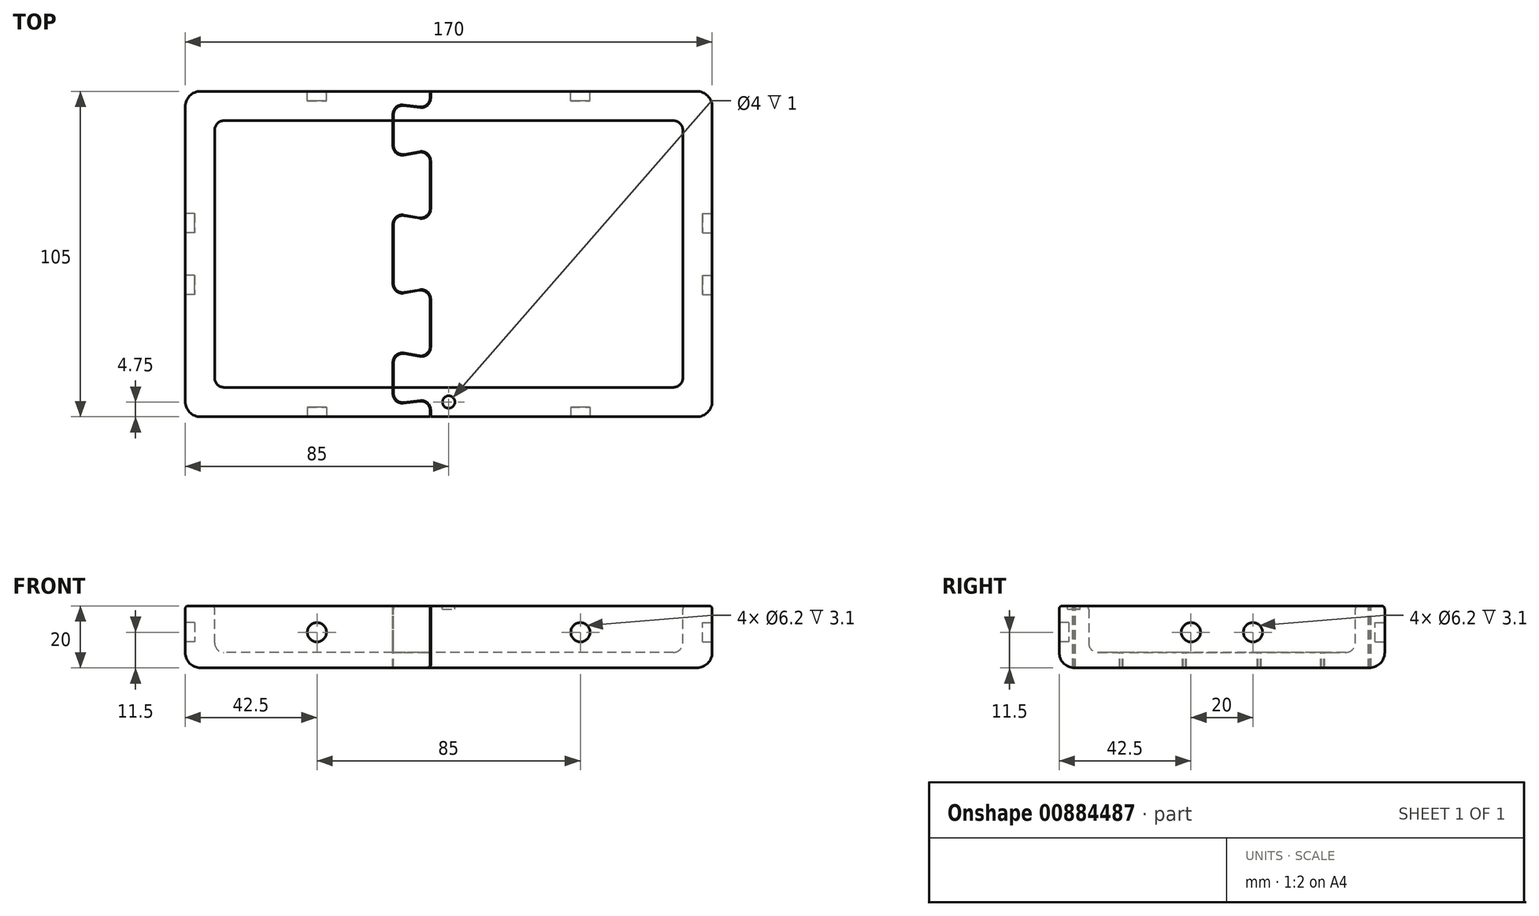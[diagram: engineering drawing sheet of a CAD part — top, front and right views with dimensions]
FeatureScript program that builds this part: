
annotation { "Feature Type Name" : "Feature", "Feature Type Description" : "" }
export const myFeature = defineFeature(function(context is Context, id is Id, definition is map)
    precondition{}
    {
        {
            var Q0;
            Q0=qCreatedBy(makeId("Top.planeOp"),FACE);
            var sketch = newSketch(context, id + "F0", { "sketchPlane" : qUnion([Q0])});
            skLineSegment(sketch, "E0.bottom", {"start": v(-85, 52.5) * mm, "end": v(85, 52.5) * mm});
            skLineSegment(sketch, "E0.top", {"start": v(-85, -52.5) * mm, "end": v(85, -52.5) * mm});
            skLineSegment(sketch, "E0.left", {"start": v(-85, 52.5) * mm, "end": v(-85, -52.5) * mm});
            skLineSegment(sketch, "E0.right", {"start": v(85, 52.5) * mm, "end": v(85, -52.5) * mm});
            skLineSegment(sketch, "E1.bottom", {"start": v(-72.5, 43) * mm, "end": v(72.5, 43) * mm});
            skLineSegment(sketch, "E1.top", {"start": v(-72.5, -43) * mm, "end": v(72.5, -43) * mm});
            skLineSegment(sketch, "E1.left", {"start": v(-75.5, 40) * mm, "end": v(-75.5, -40) * mm});
            skLineSegment(sketch, "E1.right", {"start": v(75.5, 40) * mm, "end": v(75.5, -40) * mm});
            skLineSegment(sketch, "E2.direction1", {"start": v(-75.5, -43) * mm, "end": v(15.26, -43) * mm, "construction": true});
            skPoint(sketch, "E3.visualSharp", {"position": v(-75.5, 43) * mm});
            skArc(sketch, "E3.filletArc", {"start": v(-72.5, 43) * mm, "mid": v(-74.62, 42.12) * mm, "end": v(-75.5, 40) * mm});
            skPoint(sketch, "E4.visualSharp", {"position": v(75.5, 43) * mm});
            skArc(sketch, "E4.filletArc", {"start": v(75.5, 40) * mm, "mid": v(74.62, 42.12) * mm, "end": v(72.5, 43) * mm});
            skPoint(sketch, "E5.visualSharp", {"position": v(75.5, -43) * mm});
            skArc(sketch, "E5.filletArc", {"start": v(72.5, -43) * mm, "mid": v(74.62, -42.12) * mm, "end": v(75.5, -40) * mm});
            skPoint(sketch, "E6.visualSharp", {"position": v(-75.5, -43) * mm});
            skArc(sketch, "E6.filletArc", {"start": v(-75.5, -40) * mm, "mid": v(-74.62, -42.12) * mm, "end": v(-72.5, -43) * mm});
            skLineSegment(sketch, "E7.direction1", {"start": v(-75.5, -43) * mm, "end": v(17, -43) * mm, "construction": true});
            skLineSegment(sketch, "E8", {"start": v(-85, 0) * mm, "end": v(85, 0) * mm, "construction": true});
            skLineSegment(sketch, "E9", {"start": v(0, -52.5) * mm, "end": v(0, 52.5) * mm, "construction": true});
            skCircle(sketch, "E10", {"center": v(0, -47.75) * mm, "radius": 2 * mm});
            skSolve(sketch);
        }
        {
            assignVariable(context, id + "F1", {"name" : "h", "anyValue" : 20});
        }
        {
            assignVariable(context, id + "F2", {"name" : "d", "anyValue" : 15});
        }
        {
            var Q0;
            Q0=makeQuery(id+"F0.imprint","IMPRINT",FACE,{"disambiguationData":[TD([[makeQuery(id+"F0.imprint","IMPRINT",EDGE,{"derivedFrom":sQuery(id+"F0.wireOp",EDGE,"E1.bottom")}),-1.0]])]});
            var Q1;
            Q1=makeQuery(id+"F0.imprint","IMPRINT",FACE,{"disambiguationData":[TD([[makeQuery(id+"F0.imprint","IMPRINT",EDGE,{"derivedFrom":sQuery(id+"F0.wireOp",EDGE,"E0.bottom")}),-1.0]])]});
            var Q2;
            Q2=makeQuery(id+"F0.imprint","IMPRINT",FACE,{"disambiguationData":[TD([[makeQuery(id+"F0.imprint","IMPRINT",EDGE,{"derivedFrom":sQuery(id+"F0.wireOp",EDGE,"E2.0.2.0")}),1.0]])]});
            var Q3;
            Q3=makeQuery(id+"F0.imprint","IMPRINT",FACE,{"disambiguationData":[TD([[makeQuery(id+"F0.imprint","IMPRINT",EDGE,{"derivedFrom":sQuery(id+"F0.wireOp",EDGE,"E2.0.3.0")}),1.0]])]});
            var Q4;
            Q4=makeQuery(id+"F0.imprint","IMPRINT",FACE,{"disambiguationData":[TD([[makeQuery(id+"F0.imprint","IMPRINT",EDGE,{"derivedFrom":sQuery(id+"F0.wireOp",EDGE,"E2.0.1.0")}),1.0]])]});
            var Q5;
            Q5=makeQuery(id+"F0.imprint","IMPRINT",FACE,{"disambiguationData":[TD([[makeQuery(id+"F0.imprint","IMPRINT",EDGE,{"derivedFrom":sQuery(id+"F0.wireOp",EDGE,"E7.0.1.2")}),1.0]])]});
            var Q6;
            Q6=makeQuery(id+"F0.imprint","IMPRINT",FACE,{"disambiguationData":[TD([[makeQuery(id+"F0.imprint","IMPRINT",EDGE,{"derivedFrom":sQuery(id+"F0.wireOp",EDGE,"E7.0.2.2")}),1.0]])]});
            var Q7;
            Q7=makeQuery(id+"F0.imprint","IMPRINT",FACE,{"disambiguationData":[TD([[makeQuery(id+"F0.imprint","IMPRINT",EDGE,{"derivedFrom":sQuery(id+"F0.wireOp",EDGE,"E7.0.3.2")}),1.0]])]});
            var Q8;
            Q8=makeQuery(id+"F0.imprint","IMPRINT",FACE,{"disambiguationData":[TD([[makeQuery(id+"F0.imprint","IMPRINT",EDGE,{"derivedFrom":sQuery(id+"F0.wireOp",EDGE,"E10")}),1.0]])]});
            extrude(context, id + "F3", {"entities" : qUnion([Q0, Q1, Q2, Q3, Q4, Q5, Q6, Q7, Q8]), "depth" : (getVariable(context, 'h')) * mm, "offsetDistance" : 25 * mm});
        }
        {
            var Q0;
            Q0=makeQuery(id+"F0.imprint","IMPRINT",FACE,{"disambiguationData":[TD([[makeQuery(id+"F0.imprint","IMPRINT",EDGE,{"derivedFrom":sQuery(id+"F0.wireOp",EDGE,"E1.bottom")}),-1.0]])]});
            var Q1;
            Q1=makeQuery(id+"F0.imprint","IMPRINT",FACE,{"disambiguationData":[TD([[makeQuery(id+"F0.imprint","IMPRINT",EDGE,{"derivedFrom":sQuery(id+"F0.wireOp",EDGE,"E2.0.1.0")}),1.0]])]});
            var Q2;
            Q2=makeQuery(id+"F0.imprint","IMPRINT",FACE,{"disambiguationData":[TD([[makeQuery(id+"F0.imprint","IMPRINT",EDGE,{"derivedFrom":sQuery(id+"F0.wireOp",EDGE,"E2.0.2.0")}),1.0]])]});
            var Q3;
            Q3=makeQuery(id+"F0.imprint","IMPRINT",FACE,{"disambiguationData":[TD([[makeQuery(id+"F0.imprint","IMPRINT",EDGE,{"derivedFrom":sQuery(id+"F0.wireOp",EDGE,"E2.0.3.0")}),1.0]])]});
            var Q4;
            Q4=makeQuery(id+"F0.imprint","IMPRINT",FACE,{"disambiguationData":[TD([[makeQuery(id+"F0.imprint","IMPRINT",EDGE,{"derivedFrom":sQuery(id+"F0.wireOp",EDGE,"E7.0.1.2")}),1.0]])]});
            var Q5;
            Q5=makeQuery(id+"F0.imprint","IMPRINT",FACE,{"disambiguationData":[TD([[makeQuery(id+"F0.imprint","IMPRINT",EDGE,{"derivedFrom":sQuery(id+"F0.wireOp",EDGE,"E7.0.2.2")}),1.0]])]});
            var Q6;
            Q6=makeQuery(id+"F0.imprint","IMPRINT",FACE,{"disambiguationData":[TD([[makeQuery(id+"F0.imprint","IMPRINT",EDGE,{"derivedFrom":sQuery(id+"F0.wireOp",EDGE,"E7.0.3.2")}),1.0]])]});
            extrude(context, id + "F4", {"entities" : qUnion([Q0, Q1, Q2, Q3, Q4, Q5, Q6]), "operationType" : NewBodyOperationType.REMOVE, "depth" : (getVariable(context, 'd')) * mm, "offsetDistance" : 25 * mm});
        }
        {
            var Q0;
            Q0=makeQuery(id+"F3.opExtrude","CAP_FACE",FACE,{"disambiguationData":[OSD([sQuery(id+"F0.wireOp",EDGE,"E0.bottom"),sQuery(id+"F0.wireOp",EDGE,"E0.top"),sQuery(id+"F0.wireOp",EDGE,"E0.left"),sQuery(id+"F0.wireOp",EDGE,"E0.right")])],"isStart":false});
            var Q1;
            Q1=makeQuery(id+"F3.opExtrude","SWEPT_EDGE",EDGE,{"disambiguationData":[OSD([sQuery(id+"F0.wireOp",EDGE,"E0.bottom"),sQuery(id+"F0.wireOp",EDGE,"E0.right")])]});
            var Q2;
            Q2=makeQuery(id+"F3.opExtrude","SWEPT_EDGE",EDGE,{"disambiguationData":[OSD([sQuery(id+"F0.wireOp",EDGE,"E0.bottom"),sQuery(id+"F0.wireOp",EDGE,"E0.left")])]});
            var Q3;
            Q3=makeQuery(id+"F3.opExtrude","SWEPT_EDGE",EDGE,{"disambiguationData":[OSD([sQuery(id+"F0.wireOp",EDGE,"E0.top"),sQuery(id+"F0.wireOp",EDGE,"E0.left")])]});
            var Q4;
            Q4=makeQuery(id+"F3.opExtrude","SWEPT_EDGE",EDGE,{"disambiguationData":[OSD([sQuery(id+"F0.wireOp",EDGE,"E0.top"),sQuery(id+"F0.wireOp",EDGE,"E0.right")])]});
            fillet(context, id + "F5", {"entities" : qUnion([Q0, Q1, Q2, Q3, Q4]), "radius" : 5 * mm, "tangentPropagation" : true, "allowEdgeOverflow" : false});
        }
        {
            var Q0;
            Q0=makeQuery(id+"F4.boolean.opBoolean","COPY",FACE,{"derivedFrom":makeQuery(id+"F4.opExtrude","CAP_FACE",FACE,{"disambiguationData":[OSD([sQuery(id+"F0.wireOp",EDGE,"E1.bottom"),sQuery(id+"F0.wireOp",EDGE,"E1.top"),sQuery(id+"F0.wireOp",EDGE,"E1.left"),sQuery(id+"F0.wireOp",EDGE,"E1.right"),sQuery(id+"F0.wireOp",EDGE,"E3.filletArc"),sQuery(id+"F0.wireOp",EDGE,"E4.filletArc"),sQuery(id+"F0.wireOp",EDGE,"E5.filletArc"),sQuery(id+"F0.wireOp",EDGE,"E6.filletArc")])],"isStart":false})});
            var Q1;
            Q1=makeQuery(id+"F4.boolean.opBoolean","COPY",FACE,{"derivedFrom":makeQuery(id+"F4.opExtrude","CAP_FACE",FACE,{"disambiguationData":[OSD([sQuery(id+"F0.wireOp",EDGE,"E7.0.1.2"),sQuery(id+"F0.wireOp",EDGE,"E7.0.1.4"),sQuery(id+"F0.wireOp",EDGE,"E7.0.1.5"),sQuery(id+"F0.wireOp",EDGE,"E7.0.1.6"),sQuery(id+"F0.wireOp",EDGE,"E7.0.1.7"),sQuery(id+"F0.wireOp",EDGE,"E7.0.1.9"),sQuery(id+"F0.wireOp",EDGE,"E7.0.1.11"),sQuery(id+"F0.wireOp",EDGE,"E7.0.1.12")])],"isStart":false})});
            var Q2;
            Q2=makeQuery(id+"F4.boolean.opBoolean","COPY",FACE,{"derivedFrom":makeQuery(id+"F4.opExtrude","CAP_FACE",FACE,{"disambiguationData":[OSD([sQuery(id+"F0.wireOp",EDGE,"E7.0.2.2"),sQuery(id+"F0.wireOp",EDGE,"E7.0.2.4"),sQuery(id+"F0.wireOp",EDGE,"E7.0.2.5"),sQuery(id+"F0.wireOp",EDGE,"E7.0.2.6"),sQuery(id+"F0.wireOp",EDGE,"E7.0.2.7"),sQuery(id+"F0.wireOp",EDGE,"E7.0.2.9"),sQuery(id+"F0.wireOp",EDGE,"E7.0.2.11"),sQuery(id+"F0.wireOp",EDGE,"E7.0.2.12")])],"isStart":false})});
            var Q3;
            Q3=makeQuery(id+"F4.boolean.opBoolean","COPY",FACE,{"derivedFrom":makeQuery(id+"F4.opExtrude","CAP_FACE",FACE,{"disambiguationData":[OSD([sQuery(id+"F0.wireOp",EDGE,"E7.0.3.2"),sQuery(id+"F0.wireOp",EDGE,"E7.0.3.4"),sQuery(id+"F0.wireOp",EDGE,"E7.0.3.5"),sQuery(id+"F0.wireOp",EDGE,"E7.0.3.6"),sQuery(id+"F0.wireOp",EDGE,"E7.0.3.7"),sQuery(id+"F0.wireOp",EDGE,"E7.0.3.9"),sQuery(id+"F0.wireOp",EDGE,"E7.0.3.11"),sQuery(id+"F0.wireOp",EDGE,"E7.0.3.12")])],"isStart":false})});
            fillet(context, id + "F6", {"entities" : qUnion([Q0, Q1, Q2, Q3]), "radius" : 3 * mm, "tangentPropagation" : true, "allowEdgeOverflow" : false});
        }
        {
            var Q0;
            Q0=makeQuery(id+"F3.opExtrude","CAP_FACE",FACE,{"disambiguationData":[OSD([sQuery(id+"F0.wireOp",EDGE,"E0.bottom"),sQuery(id+"F0.wireOp",EDGE,"E0.top"),sQuery(id+"F0.wireOp",EDGE,"E0.left"),sQuery(id+"F0.wireOp",EDGE,"E0.right")])],"isStart":true});
            fillet(context, id + "F7", {"entities" : qUnion([Q0]), "radius" : 1 * mm, "tangentPropagation" : true, "allowEdgeOverflow" : false});
        }
        {
            var Q0;
            Q0=makeQuery(id+"F3.opExtrude","SWEPT_FACE",FACE,{"disambiguationData":[OSD([sQuery(id+"F0.wireOp",EDGE,"E0.top")])]});
            var sketch = newSketch(context, id + "F8", { "sketchPlane" : qUnion([Q0])});
            skCircle(sketch, "E11", {"center": v(42.5, 8.5) * mm, "radius": 3.1 * mm});
            skCircle(sketch, "E12", {"center": v(-42.5, 8.5) * mm, "radius": 3.1 * mm});
            skLineSegment(sketch, "E13", {"start": v(-42.5, 8.5) * mm, "end": v(42.5, 8.5) * mm, "construction": true});
            skSolve(sketch);
        }
        {
            var Q0;
            Q0=makeQuery(id+"F8.imprint","IMPRINT",FACE,{"disambiguationData":[TD([[makeQuery(id+"F8.imprint","IMPRINT",EDGE,{"derivedFrom":sQuery(id+"F8.wireOp",EDGE,"E11")}),1.0]])]});
            var Q1;
            Q1=makeQuery(id+"F8.imprint","IMPRINT",FACE,{"disambiguationData":[TD([[makeQuery(id+"F8.imprint","IMPRINT",EDGE,{"derivedFrom":sQuery(id+"F8.wireOp",EDGE,"E12")}),1.0]])]});
            extrude(context, id + "F9", {"entities" : qUnion([Q0, Q1]), "operationType" : NewBodyOperationType.REMOVE, "oppositeDirection" : true, "depth" : 3.1 * mm, "offsetDistance" : 25 * mm});
        }
        {
            var Q0;
            Q0=makeQuery(id+"F3.opExtrude","SWEPT_FACE",FACE,{"disambiguationData":[OSD([sQuery(id+"F0.wireOp",EDGE,"E0.bottom")])]});
            var sketch = newSketch(context, id + "F10", { "sketchPlane" : qUnion([Q0])});
            skCircle(sketch, "E14", {"center": v(42.5, 8.5) * mm, "radius": 3.1 * mm});
            skCircle(sketch, "E15", {"center": v(-42.5, 8.5) * mm, "radius": 3.1 * mm});
            skLineSegment(sketch, "E16", {"start": v(42.5, 8.5) * mm, "end": v(-42.5, 8.5) * mm, "construction": true});
            skSolve(sketch);
        }
        {
            var Q0;
            Q0=makeQuery(id+"F10.imprint","IMPRINT",FACE,{"disambiguationData":[TD([[makeQuery(id+"F10.imprint","IMPRINT",EDGE,{"derivedFrom":sQuery(id+"F10.wireOp",EDGE,"E14")}),1.0]])]});
            var Q1;
            Q1=makeQuery(id+"F10.imprint","IMPRINT",FACE,{"disambiguationData":[TD([[makeQuery(id+"F10.imprint","IMPRINT",EDGE,{"derivedFrom":sQuery(id+"F10.wireOp",EDGE,"E15")}),1.0]])]});
            extrude(context, id + "F11", {"entities" : qUnion([Q0, Q1]), "operationType" : NewBodyOperationType.REMOVE, "oppositeDirection" : true, "depth" : 3.1 * mm, "offsetDistance" : 25 * mm});
        }
        {
            var Q0;
            Q0=makeQuery(id+"F3.opExtrude","SWEPT_FACE",FACE,{"disambiguationData":[OSD([sQuery(id+"F0.wireOp",EDGE,"E0.left")])]});
            var sketch = newSketch(context, id + "F12", { "sketchPlane" : qUnion([Q0])});
            skCircle(sketch, "E17", {"center": v(10, 8.5) * mm, "radius": 3.1 * mm});
            skCircle(sketch, "E18", {"center": v(-10, 8.5) * mm, "radius": 3.1 * mm});
            skLineSegment(sketch, "E19", {"start": v(-10, 8.5) * mm, "end": v(10, 8.5) * mm, "construction": true});
            skSolve(sketch);
        }
        {
            var Q0;
            Q0=makeQuery(id+"F12.imprint","IMPRINT",FACE,{"disambiguationData":[TD([[makeQuery(id+"F12.imprint","IMPRINT",EDGE,{"derivedFrom":sQuery(id+"F12.wireOp",EDGE,"E17")}),1.0]])]});
            var Q1;
            Q1=makeQuery(id+"F12.imprint","IMPRINT",FACE,{"disambiguationData":[TD([[makeQuery(id+"F12.imprint","IMPRINT",EDGE,{"derivedFrom":sQuery(id+"F12.wireOp",EDGE,"E18")}),1.0]])]});
            extrude(context, id + "F13", {"entities" : qUnion([Q0, Q1]), "operationType" : NewBodyOperationType.REMOVE, "oppositeDirection" : true, "depth" : 3.1 * mm, "offsetDistance" : 25 * mm});
        }
        {
            var Q0;
            Q0=makeQuery(id+"F3.opExtrude","SWEPT_FACE",FACE,{"disambiguationData":[OSD([sQuery(id+"F0.wireOp",EDGE,"E0.right")])]});
            var sketch = newSketch(context, id + "F14", { "sketchPlane" : qUnion([Q0])});
            skCircle(sketch, "E20", {"center": v(10, 8.5) * mm, "radius": 3.1 * mm});
            skCircle(sketch, "E21", {"center": v(-10, 8.5) * mm, "radius": 3.1 * mm});
            skLineSegment(sketch, "E22", {"start": v(10, 8.5) * mm, "end": v(-10, 8.5) * mm, "construction": true});
            skSolve(sketch);
        }
        {
            var Q0;
            Q0=makeQuery(id+"F14.imprint","IMPRINT",FACE,{"disambiguationData":[TD([[makeQuery(id+"F14.imprint","IMPRINT",EDGE,{"derivedFrom":sQuery(id+"F14.wireOp",EDGE,"E20")}),1.0]])]});
            var Q1;
            Q1=makeQuery(id+"F14.imprint","IMPRINT",FACE,{"disambiguationData":[TD([[makeQuery(id+"F14.imprint","IMPRINT",EDGE,{"derivedFrom":sQuery(id+"F14.wireOp",EDGE,"E21")}),1.0]])]});
            extrude(context, id + "F15", {"entities" : qUnion([Q0, Q1]), "operationType" : NewBodyOperationType.REMOVE, "oppositeDirection" : true, "depth" : 3.1 * mm, "offsetDistance" : 25 * mm});
        }
        {
            var Q0;
            Q0=makeQuery(id+"F0.imprint","IMPRINT",FACE,{"disambiguationData":[TD([[makeQuery(id+"F0.imprint","IMPRINT",EDGE,{"derivedFrom":sQuery(id+"F0.wireOp",EDGE,"E10")}),1.0]])]});
            var Q1;
            Q1=sQuery(id+"F0.wireOp",EDGE,"E10");
            extrude(context, id + "F16", {"entities" : qUnion([Q0]), "operationType" : NewBodyOperationType.REMOVE, "surfaceEntities" : qUnion([Q1]), "depth" : 1 * mm, "offsetDistance" : 25 * mm});
        }
        {
            var Q0;
            Q0=makeQuery(id+"F3.opExtrude","SWEPT_BODY",BODY,{"disambiguationData":[OSD([sQuery(id+"F0.wireOp",EDGE,"E0.bottom"),sQuery(id+"F0.wireOp",EDGE,"E0.top"),sQuery(id+"F0.wireOp",EDGE,"E0.left"),sQuery(id+"F0.wireOp",EDGE,"E0.right")])]});
            var Q1;
            Q1=sQuery(id+"F0.wireOp",EDGE,"E9");
            transform(context, id + "F17", {"entities" : qUnion([Q0]), "transformType" : TransformType.ROTATION, "transformAxis" : qUnion([Q1]), "angle" : 180 * degree, "makeCopy" : false});
        }
        {
            var Q0;
            Q0=qCreatedBy(makeId("Top.planeOp"),FACE);
            var sketch = newSketch(context, id + "F18", { "sketchPlane" : qUnion([Q0])});
            skLineSegment(sketch, "E23", {"start": v(-18, 0) * mm, "end": v(-18, 9.66) * mm});
            skLineSegment(sketch, "E24", {"start": v(-14.48, 12.62) * mm, "end": v(-9.52, 11.74) * mm});
            skLineSegment(sketch, "E25", {"start": v(-6, 14.7) * mm, "end": v(-6, 29.85) * mm});
            skLineSegment(sketch, "E26", {"start": v(-9.52, 32.8) * mm, "end": v(-14.48, 31.93) * mm});
            skLineSegment(sketch, "E27", {"start": v(-18, 34.89) * mm, "end": v(-18, 45.12) * mm});
            skLineSegment(sketch, "E28", {"start": v(-14.65, 48.1) * mm, "end": v(-9.35, 47.48) * mm});
            skLineSegment(sketch, "E29", {"start": v(-6, 50.46) * mm, "end": v(-6, 69.12) * mm});
            skLineSegment(sketch, "E30", {"start": v(-6, 69.12) * mm, "end": v(-107.24, 69.12) * mm});
            skLineSegment(sketch, "E31", {"start": v(-107.24, 69.12) * mm, "end": v(-107.24, 0) * mm});
            skLineSegment(sketch, "E32.MirrorCS", {"start": v(-6, -69.12) * mm, "end": v(-107.24, -69.12) * mm});
            skLineSegment(sketch, "E33.MirrorCS", {"start": v(-107.24, -69.12) * mm, "end": v(-107.24, 0) * mm});
            skLineSegment(sketch, "E34", {"start": v(-5.8, 69.12) * mm, "end": v(108.1, 69.12) * mm});
            skLineSegment(sketch, "E35", {"start": v(108.1, 69.12) * mm, "end": v(108.1, -69.12) * mm});
            skLineSegment(sketch, "E36", {"start": v(108.1, -69.12) * mm, "end": v(-5.8, -69.12) * mm});
            skLineSegment(sketch, "E37.0", {"start": v(-5.8, 50.23) * mm, "end": v(-5.8, 69.12) * mm});
            skLineSegment(sketch, "E37.1", {"start": v(-14.45, 47.88) * mm, "end": v(-9.15, 47.25) * mm});
            skLineSegment(sketch, "E37.2", {"start": v(-17.8, 35.13) * mm, "end": v(-17.8, 44.9) * mm});
            skLineSegment(sketch, "E37.3", {"start": v(-17.8, 0) * mm, "end": v(-17.8, 9.42) * mm});
            skLineSegment(sketch, "E37.4", {"start": v(-14.28, 12.38) * mm, "end": v(-9.32, 11.5) * mm});
            skLineSegment(sketch, "E37.5", {"start": v(-5.8, 14.46) * mm, "end": v(-5.8, 30.1) * mm});
            skLineSegment(sketch, "E37.6", {"start": v(-9.32, 33.05) * mm, "end": v(-14.28, 32.17) * mm});
            skPoint(sketch, "E38.visualSharp", {"position": v(-6, 47.08) * mm});
            skArc(sketch, "E38.filletArc", {"start": v(-9.35, 47.48) * mm, "mid": v(-7, 48.21) * mm, "end": v(-6, 50.46) * mm});
            skPoint(sketch, "E39.visualSharp", {"position": v(-5.8, 46.85) * mm});
            skArc(sketch, "E39.filletArc", {"start": v(-9.15, 47.25) * mm, "mid": v(-6.8, 47.99) * mm, "end": v(-5.8, 50.23) * mm});
            skPoint(sketch, "E40.visualSharp", {"position": v(-18, 48.5) * mm});
            skArc(sketch, "E40.filletArc", {"start": v(-14.65, 48.1) * mm, "mid": v(-17, 47.37) * mm, "end": v(-18, 45.12) * mm});
            skPoint(sketch, "E41.visualSharp", {"position": v(-17.8, 48.27) * mm});
            skArc(sketch, "E41.filletArc", {"start": v(-14.45, 47.88) * mm, "mid": v(-16.8, 47.14) * mm, "end": v(-17.8, 44.9) * mm});
            skPoint(sketch, "E42.visualSharp", {"position": v(-17.8, 31.55) * mm});
            skArc(sketch, "E42.filletArc", {"start": v(-17.8, 35.13) * mm, "mid": v(-16.73, 32.83) * mm, "end": v(-14.28, 32.17) * mm});
            skPoint(sketch, "E43.visualSharp", {"position": v(-18, 31.31) * mm});
            skArc(sketch, "E43.filletArc", {"start": v(-18, 34.89) * mm, "mid": v(-16.93, 32.59) * mm, "end": v(-14.48, 31.93) * mm});
            skPoint(sketch, "E44.visualSharp", {"position": v(-6, 33.43) * mm});
            skArc(sketch, "E44.filletArc", {"start": v(-6, 29.85) * mm, "mid": v(-7.07, 32.15) * mm, "end": v(-9.52, 32.8) * mm});
            skPoint(sketch, "E45.visualSharp", {"position": v(-5.8, 33.67) * mm});
            skArc(sketch, "E45.filletArc", {"start": v(-5.8, 30.1) * mm, "mid": v(-6.87, 32.39) * mm, "end": v(-9.32, 33.05) * mm});
            skPoint(sketch, "E46.visualSharp", {"position": v(-6, 11.12) * mm});
            skArc(sketch, "E46.filletArc", {"start": v(-9.52, 11.74) * mm, "mid": v(-7.07, 12.4) * mm, "end": v(-6, 14.7) * mm});
            skPoint(sketch, "E47.visualSharp", {"position": v(-5.8, 10.88) * mm});
            skArc(sketch, "E47.filletArc", {"start": v(-9.32, 11.5) * mm, "mid": v(-6.87, 12.16) * mm, "end": v(-5.8, 14.46) * mm});
            skPoint(sketch, "E48.visualSharp", {"position": v(-18, 13.24) * mm});
            skArc(sketch, "E48.filletArc", {"start": v(-14.48, 12.62) * mm, "mid": v(-16.93, 11.96) * mm, "end": v(-18, 9.66) * mm});
            skPoint(sketch, "E49.visualSharp", {"position": v(-17.8, 13) * mm});
            skArc(sketch, "E49.filletArc", {"start": v(-14.28, 12.38) * mm, "mid": v(-16.73, 11.72) * mm, "end": v(-17.8, 9.42) * mm});
            skArc(sketch, "E50.MirrorCS", {"start": v(-14.45, -47.88) * mm, "mid": v(-16.8, -47.14) * mm, "end": v(-17.8, -44.9) * mm});
            skArc(sketch, "E51.MirrorCS", {"start": v(-14.65, -48.1) * mm, "mid": v(-17, -47.37) * mm, "end": v(-18, -45.12) * mm});
            skArc(sketch, "E52.MirrorCS", {"start": v(-9.32, -11.5) * mm, "mid": v(-6.87, -12.16) * mm, "end": v(-5.8, -14.46) * mm});
            skLineSegment(sketch, "E53.MirrorCS", {"start": v(-18, -34.89) * mm, "end": v(-18, -45.12) * mm});
            skArc(sketch, "E54.MirrorCS", {"start": v(-5.8, -30.1) * mm, "mid": v(-6.87, -32.39) * mm, "end": v(-9.32, -33.05) * mm});
            skArc(sketch, "E55.MirrorCS", {"start": v(-9.15, -47.25) * mm, "mid": v(-6.8, -47.99) * mm, "end": v(-5.8, -50.23) * mm});
            skArc(sketch, "E56.MirrorCS", {"start": v(-18, -34.89) * mm, "mid": v(-16.93, -32.59) * mm, "end": v(-14.48, -31.93) * mm});
            skLineSegment(sketch, "E57.MirrorCS", {"start": v(-18, 0) * mm, "end": v(-18, -9.66) * mm});
            skArc(sketch, "E58.MirrorCS", {"start": v(-14.48, -12.62) * mm, "mid": v(-16.93, -11.96) * mm, "end": v(-18, -9.66) * mm});
            skArc(sketch, "E59.MirrorCS", {"start": v(-14.28, -12.38) * mm, "mid": v(-16.73, -11.72) * mm, "end": v(-17.8, -9.42) * mm});
            skPoint(sketch, "E60.MirrorP", {"position": v(-17.8, -48.27) * mm});
            skArc(sketch, "E61.MirrorCS", {"start": v(-9.35, -47.48) * mm, "mid": v(-7, -48.21) * mm, "end": v(-6, -50.46) * mm});
            skArc(sketch, "E62.MirrorCS", {"start": v(-9.52, -11.74) * mm, "mid": v(-7.07, -12.4) * mm, "end": v(-6, -14.7) * mm});
            skArc(sketch, "E63.MirrorCS", {"start": v(-17.8, -35.13) * mm, "mid": v(-16.73, -32.83) * mm, "end": v(-14.28, -32.17) * mm});
            skArc(sketch, "E64.MirrorCS", {"start": v(-6, -29.85) * mm, "mid": v(-7.07, -32.15) * mm, "end": v(-9.52, -32.8) * mm});
            skPoint(sketch, "E65.MirrorP", {"position": v(-18, -13.24) * mm});
            skLineSegment(sketch, "E66.MirrorCS", {"start": v(-17.8, -35.13) * mm, "end": v(-17.8, -44.9) * mm});
            skPoint(sketch, "E67.MirrorP", {"position": v(-5.8, -33.67) * mm});
            skLineSegment(sketch, "E68.MirrorCS", {"start": v(-6, -50.46) * mm, "end": v(-6, -69.12) * mm});
            skLineSegment(sketch, "E69.MirrorCS", {"start": v(-14.65, -48.1) * mm, "end": v(-9.35, -47.48) * mm});
            skPoint(sketch, "E70.MirrorP", {"position": v(-5.8, -10.88) * mm});
            skLineSegment(sketch, "E71.MirrorCS", {"start": v(-9.32, -33.05) * mm, "end": v(-14.28, -32.17) * mm});
            skPoint(sketch, "E72.MirrorP", {"position": v(-17.8, -31.55) * mm});
            skLineSegment(sketch, "E73.MirrorCS", {"start": v(-6, -14.7) * mm, "end": v(-6, -29.85) * mm});
            skPoint(sketch, "E74.MirrorP", {"position": v(-6, -11.12) * mm});
            skPoint(sketch, "E75.MirrorP", {"position": v(-18, -31.31) * mm});
            skLineSegment(sketch, "E76.MirrorCS", {"start": v(-5.8, -50.23) * mm, "end": v(-5.8, -69.12) * mm});
            skPoint(sketch, "E77.MirrorP", {"position": v(-5.8, -46.85) * mm});
            skPoint(sketch, "E78.MirrorP", {"position": v(-18, -48.5) * mm});
            skLineSegment(sketch, "E79.MirrorCS", {"start": v(-5.8, -14.46) * mm, "end": v(-5.8, -30.1) * mm});
            skLineSegment(sketch, "E80.MirrorCS", {"start": v(-14.45, -47.88) * mm, "end": v(-9.15, -47.25) * mm});
            skPoint(sketch, "E81.MirrorP", {"position": v(-6, -33.43) * mm});
            skPoint(sketch, "E82.MirrorP", {"position": v(-17.8, -13) * mm});
            skLineSegment(sketch, "E83.MirrorCS", {"start": v(-14.28, -12.38) * mm, "end": v(-9.32, -11.5) * mm});
            skPoint(sketch, "E84.MirrorP", {"position": v(-6, -47.08) * mm});
            skLineSegment(sketch, "E85.MirrorCS", {"start": v(-14.48, -12.62) * mm, "end": v(-9.52, -11.74) * mm});
            skLineSegment(sketch, "E86.MirrorCS", {"start": v(-9.52, -32.8) * mm, "end": v(-14.48, -31.93) * mm});
            skLineSegment(sketch, "E87.MirrorCS", {"start": v(-17.8, 0) * mm, "end": v(-17.8, -9.42) * mm});
            skSolve(sketch);
        }
        {
            var Q0;
            Q0=makeQuery(id+"F18.imprint","IMPRINT",FACE,{"disambiguationData":[TD([[makeQuery(id+"F18.imprint","IMPRINT",EDGE,{"derivedFrom":sQuery(id+"F18.wireOp",EDGE,"E23")}),1.0]])]});
            extrude(context, id + "F19", {"entities" : qUnion([Q0]), "oppositeDirection" : true, "depth" : 25 * mm, "offsetDistance" : 25 * mm});
        }
        {
            var Q0;
            Q0=makeQuery(id+"F18.imprint","IMPRINT",FACE,{"disambiguationData":[TD([[makeQuery(id+"F18.imprint","IMPRINT",EDGE,{"derivedFrom":sQuery(id+"F18.wireOp",EDGE,"E34")}),-1.0]])]});
            extrude(context, id + "F20", {"entities" : qUnion([Q0]), "oppositeDirection" : true, "depth" : 25 * mm, "offsetDistance" : 25 * mm});
        }
        {
            var Q0;
            Q0=makeQuery(id+"F3.opExtrude","SWEPT_BODY",BODY,{"disambiguationData":[OSD([sQuery(id+"F0.wireOp",EDGE,"E0.bottom"),sQuery(id+"F0.wireOp",EDGE,"E0.top"),sQuery(id+"F0.wireOp",EDGE,"E0.left"),sQuery(id+"F0.wireOp",EDGE,"E0.right")])]});
            transform(context, id + "F21", {"entities" : qUnion([Q0]), "transformType" : TransformType.TRANSLATION_3D, "dx" : 0 * mm, "dy" : 0 * mm, "dz" : 0 * mm, "makeCopy" : true});
        }
        {
            var Q0;
            Q0=makeQuery(id+"F3.opExtrude","SWEPT_BODY",BODY,{"disambiguationData":[OSD([sQuery(id+"F0.wireOp",EDGE,"E0.bottom"),sQuery(id+"F0.wireOp",EDGE,"E0.top"),sQuery(id+"F0.wireOp",EDGE,"E0.left"),sQuery(id+"F0.wireOp",EDGE,"E0.right")])]});
            var Q1;
            Q1=makeQuery(id+"F19.opExtrude","SWEPT_BODY",BODY,{"disambiguationData":[OSD([sQuery(id+"F18.wireOp",EDGE,"E23"),sQuery(id+"F18.wireOp",EDGE,"E24"),sQuery(id+"F18.wireOp",EDGE,"E25"),sQuery(id+"F18.wireOp",EDGE,"E26"),sQuery(id+"F18.wireOp",EDGE,"E27"),sQuery(id+"F18.wireOp",EDGE,"E28"),sQuery(id+"F18.wireOp",EDGE,"E29"),sQuery(id+"F18.wireOp",EDGE,"E30"),sQuery(id+"F18.wireOp",EDGE,"E31"),sQuery(id+"F18.wireOp",EDGE,"E32.MirrorCS"),sQuery(id+"F18.wireOp",EDGE,"E33.MirrorCS"),sQuery(id+"F18.wireOp",EDGE,"E38.filletArc"),sQuery(id+"F18.wireOp",EDGE,"E40.filletArc"),sQuery(id+"F18.wireOp",EDGE,"E43.filletArc"),sQuery(id+"F18.wireOp",EDGE,"E44.filletArc"),sQuery(id+"F18.wireOp",EDGE,"E46.filletArc"),sQuery(id+"F18.wireOp",EDGE,"E48.filletArc"),sQuery(id+"F18.wireOp",EDGE,"E51.MirrorCS"),sQuery(id+"F18.wireOp",EDGE,"E53.MirrorCS"),sQuery(id+"F18.wireOp",EDGE,"E56.MirrorCS"),sQuery(id+"F18.wireOp",EDGE,"E57.MirrorCS"),sQuery(id+"F18.wireOp",EDGE,"E58.MirrorCS"),sQuery(id+"F18.wireOp",EDGE,"E61.MirrorCS"),sQuery(id+"F18.wireOp",EDGE,"E62.MirrorCS"),sQuery(id+"F18.wireOp",EDGE,"E64.MirrorCS"),sQuery(id+"F18.wireOp",EDGE,"E68.MirrorCS"),sQuery(id+"F18.wireOp",EDGE,"E69.MirrorCS"),sQuery(id+"F18.wireOp",EDGE,"E73.MirrorCS"),sQuery(id+"F18.wireOp",EDGE,"E85.MirrorCS"),sQuery(id+"F18.wireOp",EDGE,"E86.MirrorCS")])]});
            booleanBodies(context, id + "F22", {"operationType" : BooleanOperationType.INTERSECTION, "tools" : qUnion([Q0, Q1])});
        }
        {
            var Q0;
            Q0=makeQuery(id+"F20.opExtrude","SWEPT_BODY",BODY,{"disambiguationData":[OSD([sQuery(id+"F18.wireOp",EDGE,"E34"),sQuery(id+"F18.wireOp",EDGE,"E35"),sQuery(id+"F18.wireOp",EDGE,"E36"),sQuery(id+"F18.wireOp",EDGE,"E37.0"),sQuery(id+"F18.wireOp",EDGE,"E37.1"),sQuery(id+"F18.wireOp",EDGE,"E37.2"),sQuery(id+"F18.wireOp",EDGE,"E37.3"),sQuery(id+"F18.wireOp",EDGE,"E37.4"),sQuery(id+"F18.wireOp",EDGE,"E37.5"),sQuery(id+"F18.wireOp",EDGE,"E37.6"),sQuery(id+"F18.wireOp",EDGE,"E39.filletArc"),sQuery(id+"F18.wireOp",EDGE,"E41.filletArc"),sQuery(id+"F18.wireOp",EDGE,"E42.filletArc"),sQuery(id+"F18.wireOp",EDGE,"E45.filletArc"),sQuery(id+"F18.wireOp",EDGE,"E47.filletArc"),sQuery(id+"F18.wireOp",EDGE,"E49.filletArc"),sQuery(id+"F18.wireOp",EDGE,"E50.MirrorCS"),sQuery(id+"F18.wireOp",EDGE,"E52.MirrorCS"),sQuery(id+"F18.wireOp",EDGE,"E54.MirrorCS"),sQuery(id+"F18.wireOp",EDGE,"E55.MirrorCS"),sQuery(id+"F18.wireOp",EDGE,"E59.MirrorCS"),sQuery(id+"F18.wireOp",EDGE,"E63.MirrorCS"),sQuery(id+"F18.wireOp",EDGE,"E66.MirrorCS"),sQuery(id+"F18.wireOp",EDGE,"E71.MirrorCS"),sQuery(id+"F18.wireOp",EDGE,"E76.MirrorCS"),sQuery(id+"F18.wireOp",EDGE,"E79.MirrorCS"),sQuery(id+"F18.wireOp",EDGE,"E80.MirrorCS"),sQuery(id+"F18.wireOp",EDGE,"E83.MirrorCS"),sQuery(id+"F18.wireOp",EDGE,"E87.MirrorCS")])]});
            var Q1;
            Q1=makeQuery(id+"F21.opPattern","COPY",BODY,{"derivedFrom":makeQuery(id+"F3.opExtrude","SWEPT_BODY",BODY,{"disambiguationData":[OSD([sQuery(id+"F0.wireOp",EDGE,"E0.bottom"),sQuery(id+"F0.wireOp",EDGE,"E0.top"),sQuery(id+"F0.wireOp",EDGE,"E0.left"),sQuery(id+"F0.wireOp",EDGE,"E0.right")])]}),"instanceName":"1"});
            booleanBodies(context, id + "F23", {"operationType" : BooleanOperationType.INTERSECTION, "tools" : qUnion([Q0, Q1])});
        }
    });
